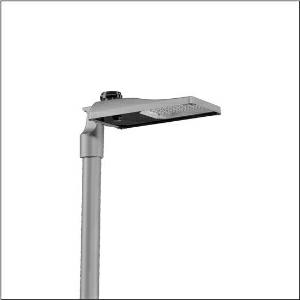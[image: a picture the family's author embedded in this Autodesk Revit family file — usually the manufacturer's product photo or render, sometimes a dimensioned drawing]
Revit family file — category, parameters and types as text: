
# Revit family: streetlight_sl_31_mini___st1_0a_5xh2d3bm08ha_2d93
name_source: partatom
category: Lighting Fixtures
units: mm (PartAtom-declared; Revit-internal decimal feet)

## family parameters
Cut with Voids When Loaded = No
Host = Face
Light Source = No
Part Type = Normal
Room Calculation Point = No
Round Connector Dimension = Use Diameter
Shared = No

## types (1)
- --- (1 x LED, 9230 lm, 68.3 W, 3000K)
    Apparent Load = 68 VA
    CIE Flux Codes = 37 72 97 100 100
    Color Rendering = 70
    Color Temperature = 3000K
    Default Elevation = 1800 mm
    Description = Streetlight SL 31 mini NEMA (7pin) mast luminaire for post-top, side-entry; light control with lens of PMMA; light distribution: ST1.0a, direct asymmetric distribution, for standard-compliant lighting for roads and squares; LED: luminous flux: 9.230lm, light colour: 730, colour temperature: 3000K; luminous efficacy: 135,1lm/W; control: pre-setting: linear dimming characteristic, flexible luminous flux parameterisation, time-dependent luminous flux control, constant luminous flux control, intelligent temperature release in ECG and LED module, overheat protection; luminaire housing, of diecast aluminium, SITECO metallic grey (DB 702S), corrosivity category C5 high according to DIN EN ISO 12944; cover of toughened safety glass, transparent, mast flange of diecast aluminium, SITECO metallic grey (DB 702S), spigot size: 76/60mm, mast flange included unmounted; cable length: 8,5m, connection cable pre-assembled; mains connection: 220..240V, AC, 50/60Hz; power consumption (at start of service life): 68,3W / (at end of service life): 74,5W / (with reduced operation 50%): 29,5W; protection rating (complete): IP66; insulation class (complete): insulation class I (protective earthing); impact resistance: IK09; certification: CE, ENEC, ENEC+, VDE, UKCA; permissible operating ambient temperature for outdoor applications: -40..+50°C; packaging unit: 1 piece

Light Distribution: ST1.0a
    Height = 76 mm
    Lamp = 1 x LED
    Lamp Light Flux = 9230 lm
    Lamp Power = 68.3 W
    Lamp count = 1
    Length = 547 mm
    Luminous efficacy = 135 lm/W
    Manufacturer = Siteco
    ModVariant = No
    Model = 5XH2D3BM08HA
    Number of Poles = 1
    OnlyDefault = Yes
    Power Factor = 1
    Product Name = Streetlight SL 31 mini | ST1.0a
    Product group = mast luminaire | pylon top
    ProductGroupID = 6100
    Protection Class = Protection class I
    Protection Degree = IP 66
    RLX_Detail_Level = 1
    RLX_Emergency_Light_Flux = 0 lm
    RLX_Emergency_Type = 0
    RLX_Emergency_Type_DB = No
    RlxData = <blob elided: 39937 chars, md5=b916659c>
    Socket = socket
    Standby Power = 0 W
    System Light Flux = 9230 lm
    System Power = 68 W
    Type Comments = factory setting: luminous flux: 100 % | dim-lin: 254 | 692 mA
    Type Image = l_1300324.jpg
    URL = http://relux.com
    VarID = @adj_020473
    Voltage = 0 V
    Weight = 0.00 kg
    Width = 265 mm

## geometry (parser evidence)
native form markers: Blend x4, Sweep x10
no freeform markers — native parametric forms only
